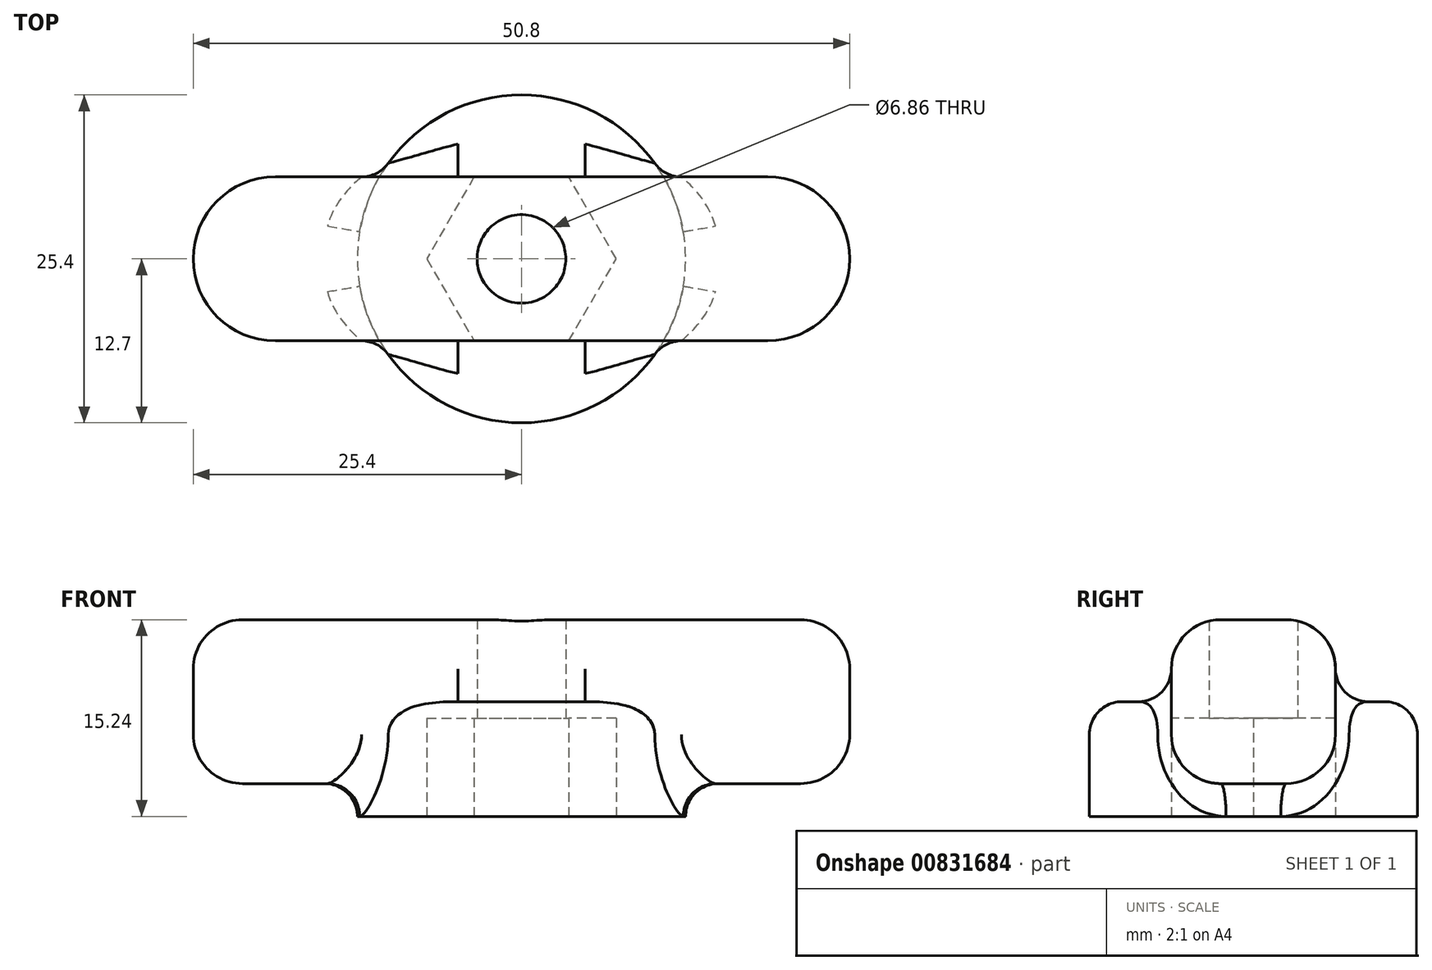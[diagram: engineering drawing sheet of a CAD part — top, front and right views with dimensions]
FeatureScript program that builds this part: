
annotation { "Feature Type Name" : "Feature", "Feature Type Description" : "" }
export const myFeature = defineFeature(function(context is Context, id is Id, definition is map)
    precondition{}
    {
        {
            var Q0;
            Q0=qCreatedBy(makeId("Top.planeOp"),FACE);
            var sketch = newSketch(context, id + "F0", { "sketchPlane" : qUnion([Q0])});
            skCircle(sketch, "E0", {"center": v(0, 0) * mm, "radius": 12.7 * mm});
            skSolve(sketch);
        }
        {
            var Q0;
            Q0=makeQuery(id+"F0.imprint","IMPRINT",FACE,{"disambiguationData":[TD([[makeQuery(id+"F0.imprint","IMPRINT",EDGE,{"derivedFrom":sQuery(id+"F0.wireOp",EDGE,"E0")}),1.0]])]});
            extrude(context, id + "F1", {"entities" : qUnion([Q0]), "depth" : 8.9 * mm, "offsetDistance" : 25.4 * mm});
        }
        {
            var Q0;
            Q0=makeQuery(id+"F1.opExtrude","CAP_FACE",FACE,{"disambiguationData":[OSD([sQuery(id+"F0.wireOp",EDGE,"E0")])],"isStart":false});
            var sketch = newSketch(context, id + "F2", { "sketchPlane" : qUnion([Q0])});
            skLineSegment(sketch, "E1.bottom", {"start": v(-25.4, 6.35) * mm, "end": v(25.4, 6.35) * mm});
            skLineSegment(sketch, "E1.top", {"start": v(-25.4, -6.35) * mm, "end": v(25.4, -6.35) * mm});
            skLineSegment(sketch, "E1.left", {"start": v(-25.4, 6.35) * mm, "end": v(-25.4, -6.35) * mm});
            skLineSegment(sketch, "E1.right", {"start": v(25.4, 6.35) * mm, "end": v(25.4, -6.35) * mm});
            skPoint(sketch, "E1.middle", {"position": v(0, 0) * mm});
            skSolve(sketch);
        }
        {
            var Q0;
            {var subQ0=sQuery(id+"F2.wireOp",EDGE,"E1.left");Q0=makeQuery(id+"F2.imprint","IMPRINT",FACE,{"disambiguationData":[TD([[makeQuery(id+"F2.imprint","IMPRINT",EDGE,{"derivedFrom":subQ0}),1.0]])]});}
            var Q1;
            {var subQ0=sQuery(id+"F2.wireOp",EDGE,"E1.bottom");var subQ1=makeQuery(id+"F1.opExtrude","CAP_EDGE",EDGE,{"disambiguationData":[OSD([sQuery(id+"F0.wireOp",EDGE,"E0")])],"isStart":false});var subQ2=makeQuery(id+"F2.imprint","INTERSECT",VERTEX,{"disambiguationData":[OD(0.0)],"derivedFrom":[subQ1,subQ0]});Q1=makeQuery(id+"F2.imprint","IMPRINT",FACE,{"disambiguationData":[TD([[makeQuery(id+"F2.imprint","IMPRINT",EDGE,{"disambiguationData":[TD([[subQ2,-1.0]])],"derivedFrom":subQ0}),-1.0]])]});}
            var Q2;
            {var subQ0=sQuery(id+"F2.wireOp",EDGE,"E1.right");Q2=makeQuery(id+"F2.imprint","IMPRINT",FACE,{"disambiguationData":[TD([[makeQuery(id+"F2.imprint","IMPRINT",EDGE,{"derivedFrom":subQ0}),-1.0]])]});}
            extrude(context, id + "F3", {"entities" : qUnion([Q0, Q1, Q2]), "operationType" : NewBodyOperationType.ADD, "depth" : 6.35 * mm, "offsetDistance" : 25.4 * mm, "hasSecondDirection" : true, "secondDirectionOppositeDirection" : true, "secondDirectionDepth" : 6.35 * mm});
        }
        {
            var Q0;
            Q0=makeQuery(id+"F1.opExtrude","CAP_FACE",FACE,{"disambiguationData":[OSD([sQuery(id+"F0.wireOp",EDGE,"E0")])],"isStart":true});
            var sketch = newSketch(context, id + "F4", { "sketchPlane" : qUnion([Q0])});
            skCircle(sketch, "E2.cCircle", {"center": v(0, 0) * mm, "radius": 6.35 * mm, "construction": true});
            skLineSegment(sketch, "E2.0", {"start": v(-3.67, 6.35) * mm, "end": v(3.67, 6.35) * mm});
            skLineSegment(sketch, "E2.1", {"start": v(3.67, 6.35) * mm, "end": v(7.33, 0) * mm});
            skLineSegment(sketch, "E2.2", {"start": v(7.33, 0) * mm, "end": v(3.67, -6.35) * mm});
            skLineSegment(sketch, "E2.3", {"start": v(3.67, -6.35) * mm, "end": v(-3.67, -6.35) * mm});
            skLineSegment(sketch, "E2.4", {"start": v(-3.67, -6.35) * mm, "end": v(-7.33, 0) * mm});
            skLineSegment(sketch, "E2.5", {"start": v(-7.33, 0) * mm, "end": v(-3.67, 6.35) * mm});
            skPoint(sketch, "E2.0.midPoint", {"position": v(0, 6.35) * mm});
            skSolve(sketch);
        }
        {
            var Q0;
            Q0=makeQuery(id+"F4.imprint","IMPRINT",FACE,{"disambiguationData":[TD([[makeQuery(id+"F4.imprint","IMPRINT",EDGE,{"derivedFrom":sQuery(id+"F4.wireOp",EDGE,"E2.0")}),-1.0]])]});
            extrude(context, id + "F5", {"entities" : qUnion([Q0]), "operationType" : NewBodyOperationType.REMOVE, "oppositeDirection" : true, "depth" : 7.62 * mm, "offsetDistance" : 25.4 * mm});
        }
        {
            var Q0;
            Q0=makeQuery(id+"F3.opExtrude","SWEPT_EDGE",EDGE,{"disambiguationData":[OSD([sQuery(id+"F2.wireOp",EDGE,"E1.bottom"),sQuery(id+"F2.wireOp",EDGE,"E1.right")])]});
            var Q1;
            Q1=makeQuery(id+"F3.opExtrude","SWEPT_EDGE",EDGE,{"disambiguationData":[OSD([sQuery(id+"F2.wireOp",EDGE,"E1.top"),sQuery(id+"F2.wireOp",EDGE,"E1.right")])]});
            var Q2;
            Q2=makeQuery(id+"F3.opExtrude","SWEPT_EDGE",EDGE,{"disambiguationData":[OSD([sQuery(id+"F2.wireOp",EDGE,"E1.bottom"),sQuery(id+"F2.wireOp",EDGE,"E1.left")])]});
            var Q3;
            Q3=makeQuery(id+"F3.opExtrude","SWEPT_EDGE",EDGE,{"disambiguationData":[OSD([sQuery(id+"F2.wireOp",EDGE,"E1.top"),sQuery(id+"F2.wireOp",EDGE,"E1.left")])]});
            fillet(context, id + "F6", {"entities" : qUnion([Q0, Q1, Q2, Q3]), "radius" : 6.35 * mm, "tangentPropagation" : true, "allowEdgeOverflow" : false});
        }
        {
            var Q0;
            Q0=makeQuery(id+"F3.opExtrude","CAP_EDGE",EDGE,{"disambiguationData":[OSD([sQuery(id+"F2.wireOp",EDGE,"E1.bottom")])],"isStart":false});
            var Q1;
            {var subQ0=sQuery(id+"F2.wireOp",EDGE,"E1.bottom");var subQ1=sQuery(id+"F2.wireOp",EDGE,"E1.right");Q1=makeQuery(id+"F3.boolean.opBoolean","SPLIT",EDGE,{"disambiguationData":[TD([makeQuery(id+"F3.opExtrude","SWEPT_FACE",FACE,{"disambiguationData":[OSD([subQ1])]})])],"derivedFrom":makeQuery(id+"F3.opExtrude","CAP_EDGE",EDGE,{"disambiguationData":[OSD([subQ0])],"isStart":true})});}
            var Q2;
            {var subQ0=sQuery(id+"F2.wireOp",EDGE,"E1.bottom");var subQ1=sQuery(id+"F2.wireOp",EDGE,"E1.left");Q2=makeQuery(id+"F3.boolean.opBoolean","SPLIT",EDGE,{"disambiguationData":[TD([makeQuery(id+"F3.opExtrude","SWEPT_FACE",FACE,{"disambiguationData":[OSD([subQ1])]})])],"derivedFrom":makeQuery(id+"F3.opExtrude","CAP_EDGE",EDGE,{"disambiguationData":[OSD([subQ0])],"isStart":true})});}
            fillet(context, id + "F7", {"entities" : qUnion([Q0, Q1, Q2]), "radius" : 3.8 * mm, "tangentPropagation" : true, "allowEdgeOverflow" : false});
        }
        {
            var Q0;
            Q0=makeQuery(id+"F3.boolean.opBoolean","INTERSECT",EDGE,{"derivedFrom":[makeQuery(id+"F1.opExtrude","CAP_FACE",FACE,{"disambiguationData":[OSD([sQuery(id+"F0.wireOp",EDGE,"E0")])],"isStart":false}),makeQuery(id+"F3.opExtrude","SWEPT_FACE",FACE,{"disambiguationData":[OSD([sQuery(id+"F2.wireOp",EDGE,"E1.top")])]})]});
            var Q1;
            Q1=makeQuery(id+"F3.boolean.opBoolean","INTERSECT",EDGE,{"derivedFrom":[makeQuery(id+"F1.opExtrude","CAP_FACE",FACE,{"disambiguationData":[OSD([sQuery(id+"F0.wireOp",EDGE,"E0")])],"isStart":false}),makeQuery(id+"F3.opExtrude","SWEPT_FACE",FACE,{"disambiguationData":[OSD([sQuery(id+"F2.wireOp",EDGE,"E1.bottom")])]})]});
            var Q2;
            {var subQ0=makeQuery(id+"F1.opExtrude","SWEPT_FACE",FACE,{"disambiguationData":[OSD([sQuery(id+"F0.wireOp",EDGE,"E0")])]});var subQ1=sQuery(id+"F2.wireOp",EDGE,"E1.bottom");var subQ2=sQuery(id+"F2.wireOp",EDGE,"E1.left");Q2=makeQuery(id+"F7.opFillet","BLEND_EDGE",EDGE,{"blendedFrom":[makeQuery(id+"F3.boolean.opBoolean","SPLIT",EDGE,{"disambiguationData":[TD([makeQuery(id+"F3.opExtrude","SWEPT_FACE",FACE,{"disambiguationData":[OSD([subQ2])]})])],"derivedFrom":makeQuery(id+"F3.opExtrude","CAP_EDGE",EDGE,{"disambiguationData":[OSD([subQ1])],"isStart":true})}),subQ0],"blendedInto":[subQ0]});}
            var Q3;
            {var subQ0=makeQuery(id+"F1.opExtrude","SWEPT_FACE",FACE,{"disambiguationData":[OSD([sQuery(id+"F0.wireOp",EDGE,"E0")])]});var subQ1=sQuery(id+"F2.wireOp",EDGE,"E1.top");var subQ2=sQuery(id+"F2.wireOp",EDGE,"E1.right");Q3=makeQuery(id+"F7.opFillet","BLEND_EDGE",EDGE,{"blendedFrom":[makeQuery(id+"F3.boolean.opBoolean","SPLIT",EDGE,{"disambiguationData":[TD([makeQuery(id+"F3.opExtrude","SWEPT_FACE",FACE,{"disambiguationData":[OSD([subQ2])]})])],"derivedFrom":makeQuery(id+"F3.opExtrude","CAP_EDGE",EDGE,{"disambiguationData":[OSD([subQ1])],"isStart":true})}),subQ0],"blendedInto":[subQ0]});}
            var Q4;
            {var subQ0=sQuery(id+"F0.wireOp",EDGE,"E0");Q4=makeQuery(id+"F3.boolean.opBoolean","SPLIT",EDGE,{"disambiguationData":[TD([makeQuery(id+"F3.opExtrude","SWEPT_FACE",FACE,{"disambiguationData":[OSD([sQuery(id+"F2.wireOp",EDGE,"E1.bottom")])]})])],"derivedFrom":makeQuery(id+"F1.opExtrude","CAP_EDGE",EDGE,{"disambiguationData":[OSD([subQ0])],"isStart":false})});}
            var Q5;
            {var subQ0=sQuery(id+"F0.wireOp",EDGE,"E0");Q5=makeQuery(id+"F3.boolean.opBoolean","SPLIT",EDGE,{"disambiguationData":[TD([makeQuery(id+"F3.opExtrude","SWEPT_FACE",FACE,{"disambiguationData":[OSD([sQuery(id+"F2.wireOp",EDGE,"E1.top")])]})])],"derivedFrom":makeQuery(id+"F1.opExtrude","CAP_EDGE",EDGE,{"disambiguationData":[OSD([subQ0])],"isStart":false})});}
            fillet(context, id + "F8", {"entities" : qUnion([Q0, Q1, Q2, Q3, Q4, Q5]), "radius" : 2.54 * mm, "tangentPropagation" : true, "allowEdgeOverflow" : false});
        }
        {
            var Q0;
            Q0=makeQuery(id+"F1.opExtrude","CAP_FACE",FACE,{"disambiguationData":[OSD([sQuery(id+"F0.wireOp",EDGE,"E0")])],"isStart":true});
            var sketch = newSketch(context, id + "F9", { "sketchPlane" : qUnion([Q0])});
            skCircle(sketch, "E3", {"center": v(0, 0) * mm, "radius": 3.43 * mm});
            skSolve(sketch);
        }
        {
            var Q0;
            Q0=makeQuery(id+"F9.imprint","IMPRINT",FACE,{"disambiguationData":[TD([[makeQuery(id+"F9.imprint","IMPRINT",EDGE,{"derivedFrom":sQuery(id+"F9.wireOp",EDGE,"E3")}),1.0]])]});
            extrude(context, id + "F10", {"entities" : qUnion([Q0]), "operationType" : NewBodyOperationType.REMOVE, "oppositeDirection" : true, "depth" : 25.4 * mm, "offsetDistance" : 25.4 * mm});
        }
    });
